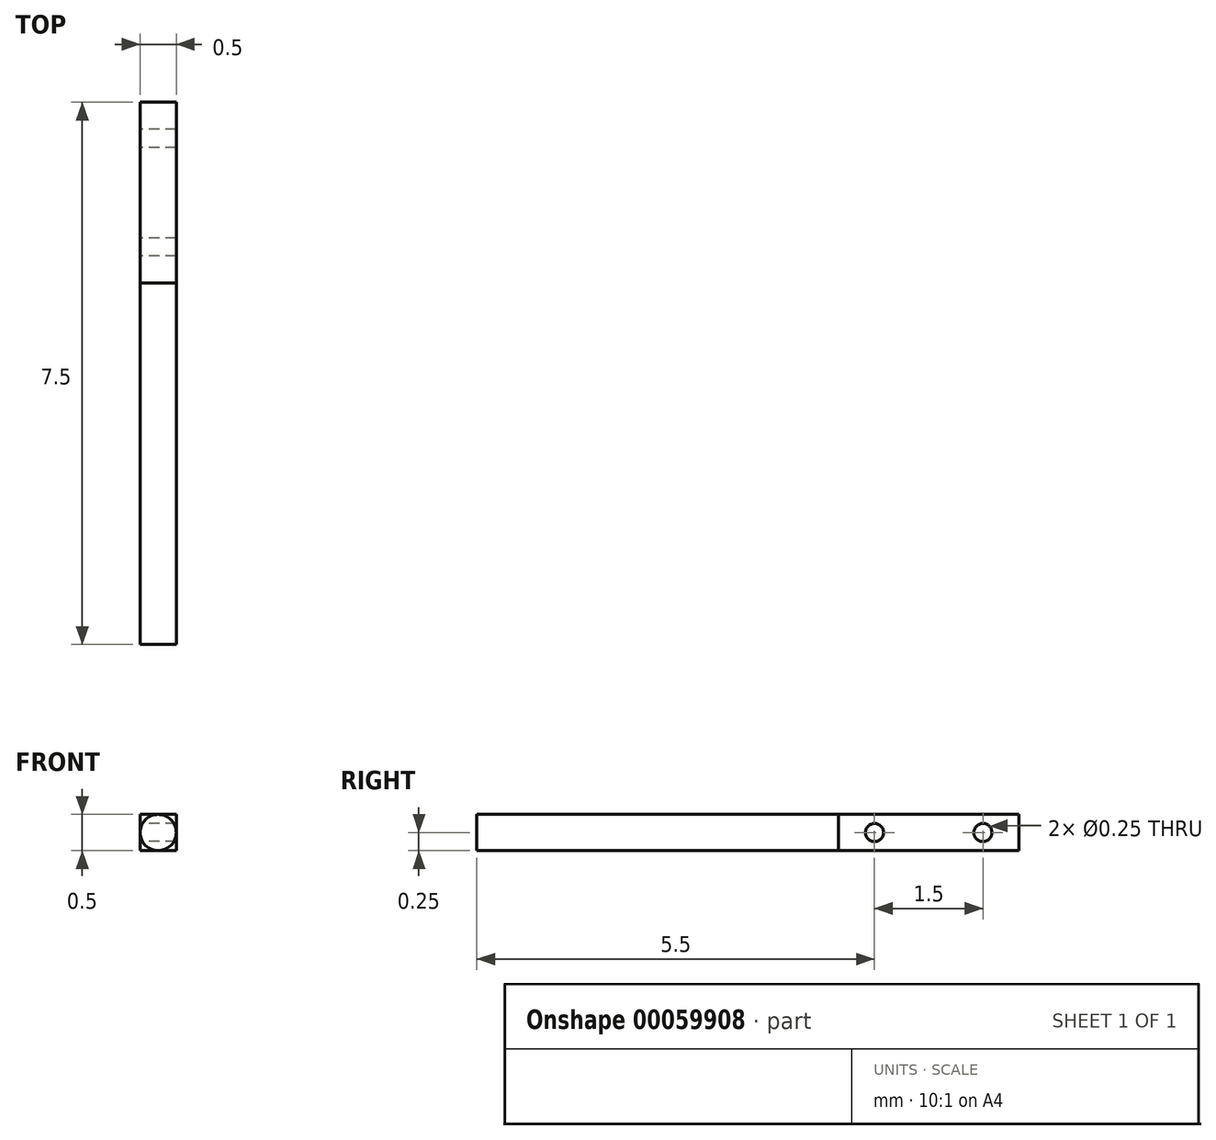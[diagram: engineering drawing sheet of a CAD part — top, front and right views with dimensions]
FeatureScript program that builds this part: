
annotation { "Feature Type Name" : "Feature", "Feature Type Description" : "" }
export const myFeature = defineFeature(function(context is Context, id is Id, definition is map)
    precondition{}
    {
        {
            var Q0;
            Q0=qCreatedBy(makeId("Front.planeOp"),FACE);
            var sketch = newSketch(context, id + "F0", { "sketchPlane" : qUnion([Q0])});
            skCircle(sketch, "E0", {"center": v(0, 0) * mm, "radius": 0.25 * mm});
            skSolve(sketch);
        }
        {
            var Q0;
            Q0 = qSketchRegion(id + "F0", true);
            extrude(context, id + "F1", {"entities" : qUnion([Q0]), "depth" : 5 * mm});
        }
        {
            var Q0;
            Q0=qCreatedBy(makeId("Front.planeOp"),FACE);
            var sketch = newSketch(context, id + "F2", { "sketchPlane" : qUnion([Q0])});
            skLineSegment(sketch, "E1.rect.bottom", {"start": v(0.25, 0.25) * mm, "end": v(-0.25, 0.25) * mm});
            skLineSegment(sketch, "E1.rect.top", {"start": v(0.25, -0.25) * mm, "end": v(-0.25, -0.25) * mm});
            skLineSegment(sketch, "E1.rect.left", {"start": v(0.25, 0.25) * mm, "end": v(0.25, -0.25) * mm});
            skLineSegment(sketch, "E1.rect.right", {"start": v(-0.25, 0.25) * mm, "end": v(-0.25, -0.25) * mm});
            skPoint(sketch, "E1.rect.middle", {"position": v(0, 0) * mm});
            skSolve(sketch);
        }
        {
            var Q0;
            Q0 = qSketchRegion(id + "F2", true);
            extrude(context, id + "F3", {"entities" : qUnion([Q0]), "operationType" : NewBodyOperationType.ADD, "oppositeDirection" : true, "depth" : 2.5 * mm});
        }
        {
            var Q0;
            Q0=makeQuery(id+"F3.opExtrude","SWEPT_FACE",FACE,{"disambiguationData":[OSD([sQuery(id+"F2.wireOp",EDGE,"E1.rect.right")])]});
            var sketch = newSketch(context, id + "F4", { "sketchPlane" : qUnion([Q0])});
            skCircle(sketch, "E2", {"center": v(-2, 0) * mm, "radius": 0.12 * mm});
            skCircle(sketch, "E3", {"center": v(-0.5, 0) * mm, "radius": 0.12 * mm});
            skSolve(sketch);
        }
        {
            var Q0;
            Q0 = qSketchRegion(id + "F4", true);
            extrude(context, id + "F5", {"entities" : qUnion([Q0]), "operationType" : NewBodyOperationType.REMOVE, "endBound" : BoundingType.THROUGH_ALL, "oppositeDirection" : true, "depth" : 25 * mm});
        }
    });
